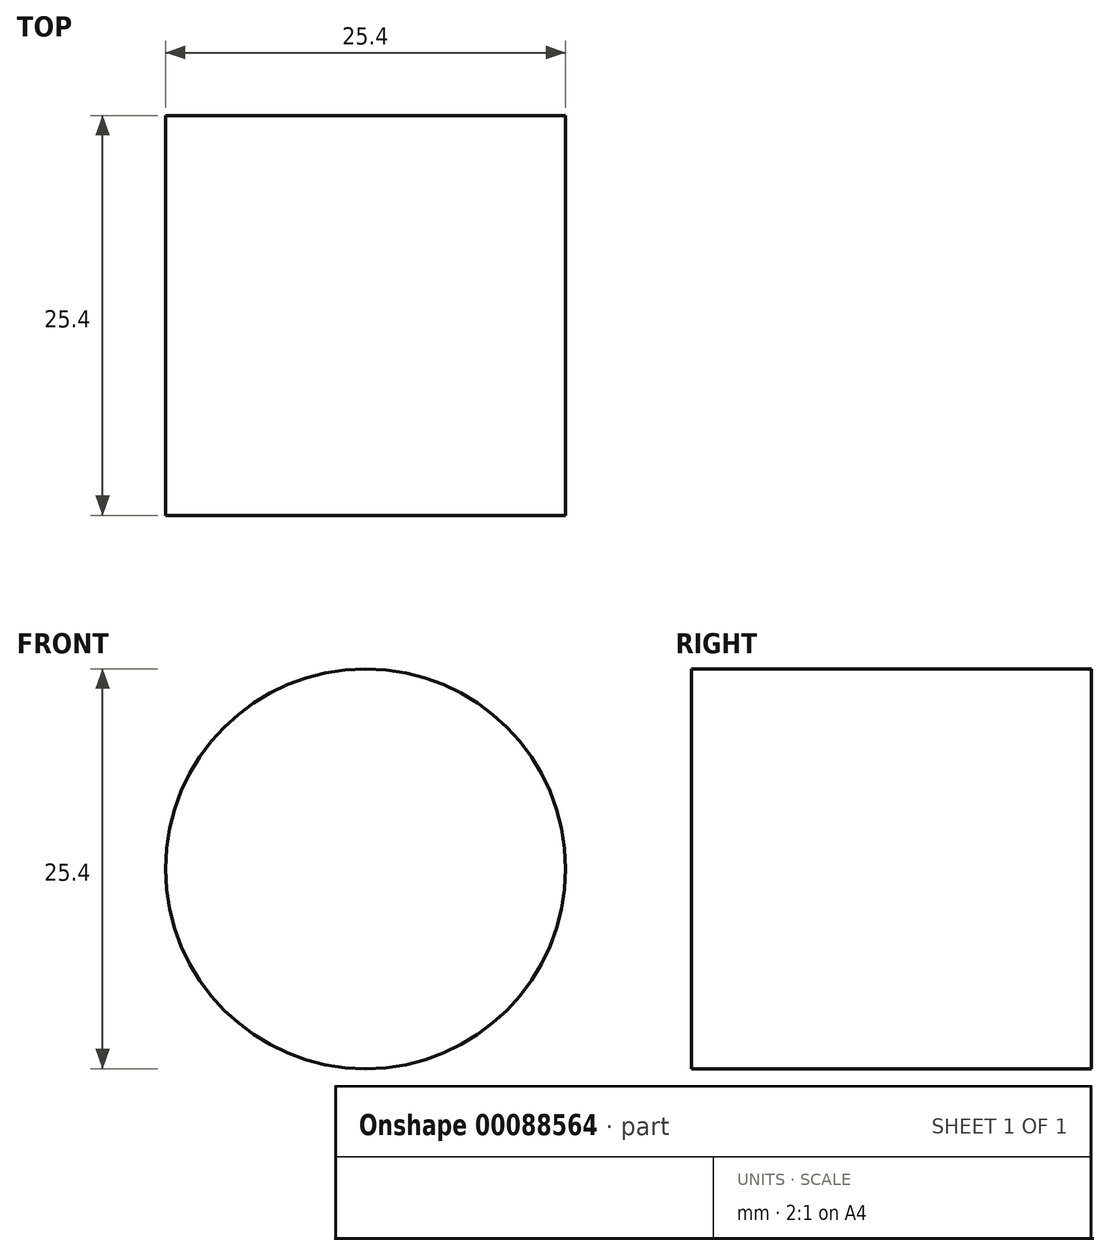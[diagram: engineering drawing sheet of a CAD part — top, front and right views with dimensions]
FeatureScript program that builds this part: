
annotation { "Feature Type Name" : "Feature", "Feature Type Description" : "" }
export const myFeature = defineFeature(function(context is Context, id is Id, definition is map)
    precondition{}
    {
        {
            var Q0;
            Q0=qCreatedBy(makeId("Front.planeOp"),FACE);
            var sketch = newSketch(context, id + "F0", { "sketchPlane" : qUnion([Q0])});
            skCircle(sketch, "E0", {"center": v(-6.45, 9.68) * mm, "radius": 12.7 * mm});
            skSolve(sketch);
        }
        {
            var Q0;
            Q0=sQuery(id+"F0.wireOp",EDGE,"E0");
            extrude(context, id + "F1", {"bodyType" : ToolBodyType.SURFACE, "surfaceEntities" : qUnion([Q0]), "endBound" : BoundingType.SYMMETRIC, "depth" : 25.4 * mm});
        }
    });
